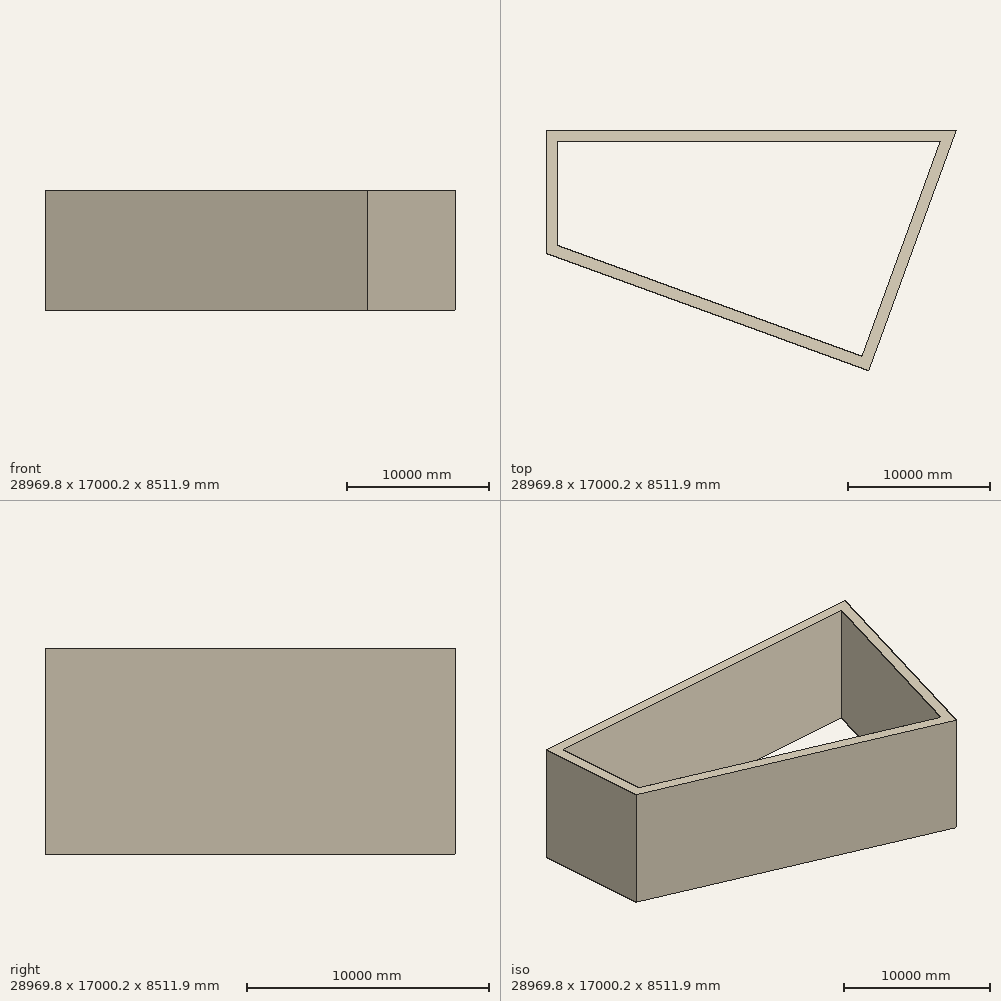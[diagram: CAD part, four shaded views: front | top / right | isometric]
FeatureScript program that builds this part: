
annotation { "Feature Type Name" : "Feature", "Feature Type Description" : "" }
export const myFeature = defineFeature(function(context is Context, id is Id, definition is map)
    precondition{}
    {
        {
            var Q0;
            Q0=qCreatedBy(makeId("Top.planeOp"),FACE);
            var sketch = newSketch(context, id + "F0", { "sketchPlane" : qUnion([Q0])});
            skLineSegment(sketch, "E0", {"start": v(-13513.5, 0) * mm, "end": v(13513.5, 0) * mm});
            skLineSegment(sketch, "E1", {"start": v(13513.5, 0) * mm, "end": v(7986.84, -15174.93) * mm});
            skLineSegment(sketch, "E2", {"start": v(-13513.5, -7350) * mm, "end": v(-13513.5, 0) * mm});
            skLineSegment(sketch, "E3", {"start": v(-13513.5, -7350) * mm, "end": v(7986.84, -15174.93) * mm});
            skLineSegment(sketch, "E4.0", {"start": v(-14313.5, -7910.18) * mm, "end": v(-14313.5, 800) * mm});
            skLineSegment(sketch, "E4.1", {"start": v(-14313.5, -7910.18) * mm, "end": v(8464.84, -16200.23) * mm});
            skLineSegment(sketch, "E4.2", {"start": v(14656.26, 800) * mm, "end": v(8464.84, -16200.23) * mm});
            skLineSegment(sketch, "E4.3", {"start": v(-14313.5, 800) * mm, "end": v(14656.26, 800) * mm});
            skSolve(sketch);
        }
        {
            var Q0;
            Q0=makeQuery(id+"F0.imprint","IMPRINT",FACE,{"disambiguationData":[TD([[makeQuery(id+"F0.imprint","IMPRINT",EDGE,{"derivedFrom":sQuery(id+"F0.wireOp",EDGE,"E0")}),1.0]])]});
            extrude(context, id + "F1", {"entities" : qUnion([Q0]), "depth" : 8511.85 * mm});
        }
    });
